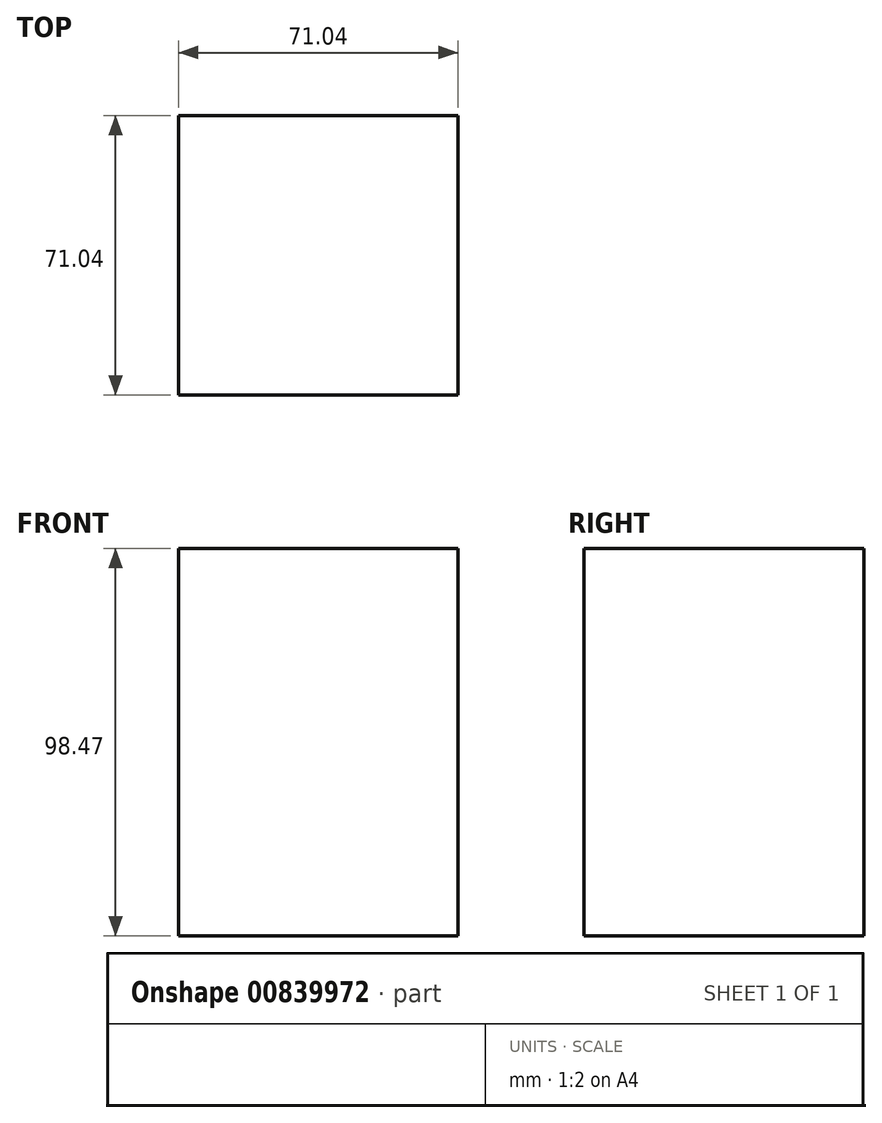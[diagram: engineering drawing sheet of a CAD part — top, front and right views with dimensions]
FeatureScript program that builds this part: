
annotation { "Feature Type Name" : "Feature", "Feature Type Description" : "" }
export const myFeature = defineFeature(function(context is Context, id is Id, definition is map)
    precondition{}
    {
        {
            var Q0;
            Q0=qCreatedBy(makeId("Top.planeOp"),FACE);
            var sketch = newSketch(context, id + "F0", { "sketchPlane" : qUnion([Q0])});
            skCircle(sketch, "E0.cCircle", {"center": v(0, 0) * mm, "radius": 35.52 * mm, "construction": true});
            skLineSegment(sketch, "E0.0", {"start": v(-35.52, 35.52) * mm, "end": v(35.52, 35.52) * mm});
            skLineSegment(sketch, "E0.1", {"start": v(35.52, 35.52) * mm, "end": v(35.52, -35.52) * mm});
            skLineSegment(sketch, "E0.2", {"start": v(35.52, -35.52) * mm, "end": v(-35.52, -35.52) * mm});
            skLineSegment(sketch, "E0.3", {"start": v(-35.52, -35.52) * mm, "end": v(-35.52, 35.52) * mm});
            skPoint(sketch, "E0.0.midPoint", {"position": v(0, 35.52) * mm});
            skSolve(sketch);
        }
        {
            var Q0;
            Q0=sQuery(id+"F0.wireOp",EDGE,"E0.0");
            var Q1;
            Q1=sQuery(id+"F0.wireOp",EDGE,"E0.3");
            var Q2;
            Q2=sQuery(id+"F0.wireOp",EDGE,"E0.1");
            var Q3;
            Q3=sQuery(id+"F0.wireOp",EDGE,"E0.2");
            extrude(context, id + "F1", {"bodyType" : ToolBodyType.SURFACE, "surfaceEntities" : qUnion([Q0, Q1, Q2, Q3]), "depth" : 98.47 * mm, "offsetDistance" : 25.4 * mm});
        }
    });
